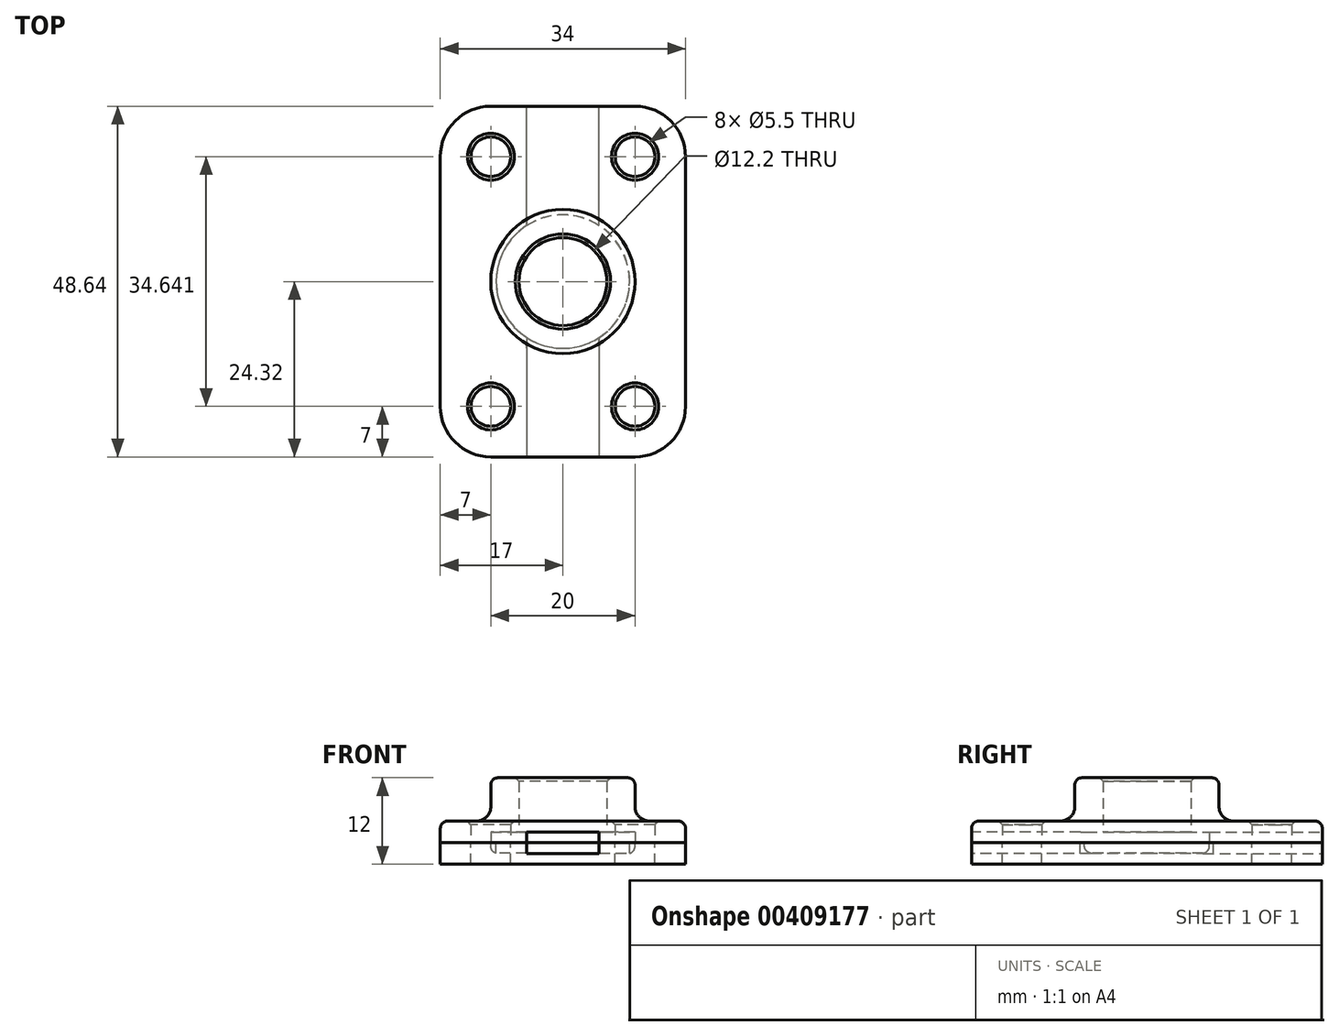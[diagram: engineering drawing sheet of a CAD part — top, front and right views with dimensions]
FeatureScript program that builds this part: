
annotation { "Feature Type Name" : "Feature", "Feature Type Description" : "" }
export const myFeature = defineFeature(function(context is Context, id is Id, definition is map)
    precondition{}
    {
        {
            var Q0;
            Q0=qCreatedBy(makeId("Top.planeOp"),FACE);
            var sketch = newSketch(context, id + "F0", { "sketchPlane" : qUnion([Q0])});
            skCircle(sketch, "E0", {"center": v(-20, 0) * mm, "radius": 2.75 * mm});
            skCircle(sketch, "E1", {"center": v(-10, 17.32) * mm, "radius": 10 * mm});
            skCircle(sketch, "E2", {"center": v(-10, 17.32) * mm, "radius": 6.1 * mm});
            skCircle(sketch, "E3", {"center": v(-10, 17.32) * mm, "radius": 5 * mm});
            skLineSegment(sketch, "E4", {"start": v(-20, 0) * mm, "end": v(-10, 17.32) * mm, "construction": true});
            skLineSegment(sketch, "E5", {"start": v(-10, 17.32) * mm, "end": v(0, 0) * mm, "construction": true});
            skLineSegment(sketch, "E6", {"start": v(-20, 0) * mm, "end": v(0, 0) * mm, "construction": true});
            skArc(sketch, "E7", {"start": v(-27, 0) * mm, "mid": v(-24.95, -4.95) * mm, "end": v(-20, -7) * mm});
            skLineSegment(sketch, "E8", {"start": v(-10, 17.32) * mm, "end": v(-10, 0) * mm, "construction": true});
            skLineSegment(sketch, "E9", {"start": v(-27, 17.32) * mm, "end": v(-27, 0) * mm});
            skLineSegment(sketch, "E10", {"start": v(-20, -7) * mm, "end": v(-10, -7) * mm});
            skLineSegment(sketch, "E11", {"start": v(-15, 8.66) * mm, "end": v(-15, -7) * mm});
            skLineSegment(sketch, "E12.MirrorCS", {"start": v(-5, 8.66) * mm, "end": v(-5, -7) * mm});
            skCircle(sketch, "E13", {"center": v(-10, 17.32) * mm, "radius": 9.25 * mm});
            skLineSegment(sketch, "E14.MirrorCS", {"start": v(0, 0) * mm, "end": v(-10, 17.32) * mm, "construction": true});
            skArc(sketch, "E15.MirrorCS", {"start": v(7, 0) * mm, "mid": v(4.95, -4.95) * mm, "end": v(0, -7) * mm});
            skLineSegment(sketch, "E16.MirrorCS", {"start": v(0, -7) * mm, "end": v(-10, -7) * mm});
            skLineSegment(sketch, "E17.MirrorCS", {"start": v(7, 17.32) * mm, "end": v(7, 0) * mm});
            skCircle(sketch, "E18.MirrorC", {"center": v(0, 0) * mm, "radius": 2.75 * mm});
            skLineSegment(sketch, "E19", {"start": v(-27, 17.32) * mm, "end": v(-10, 17.32) * mm, "construction": true});
            skLineSegment(sketch, "E20.MirrorCS", {"start": v(-27, 17.32) * mm, "end": v(-27, 34.64) * mm});
            skArc(sketch, "E21.MirrorCS", {"start": v(-27, 34.64) * mm, "mid": v(-24.95, 39.6) * mm, "end": v(-20, 41.64) * mm});
            skCircle(sketch, "E22.MirrorC", {"center": v(-20, 34.64) * mm, "radius": 2.75 * mm});
            skLineSegment(sketch, "E23.MirrorCS", {"start": v(-15, 25.98) * mm, "end": v(-15, 41.64) * mm});
            skLineSegment(sketch, "E24.MirrorCS", {"start": v(-5, 25.98) * mm, "end": v(-5, 41.64) * mm});
            skCircle(sketch, "E25.MirrorC", {"center": v(0, 34.64) * mm, "radius": 2.75 * mm});
            skLineSegment(sketch, "E26.MirrorCS", {"start": v(7, 17.32) * mm, "end": v(7, 34.64) * mm});
            skArc(sketch, "E27.MirrorCS", {"start": v(7, 34.64) * mm, "mid": v(4.95, 39.6) * mm, "end": v(0, 41.64) * mm});
            skLineSegment(sketch, "E28.MirrorCS", {"start": v(-20, 41.64) * mm, "end": v(-10, 41.64) * mm});
            skLineSegment(sketch, "E29.MirrorCS", {"start": v(0, 41.64) * mm, "end": v(-10, 41.64) * mm});
            skSolve(sketch);
        }
        {
            var Q0;
            Q0=makeQuery(id+"F0.imprint","IMPRINT",FACE,{"disambiguationData":[TD([[makeQuery(id+"F0.imprint","IMPRINT",EDGE,{"derivedFrom":sQuery(id+"F0.wireOp",EDGE,"E0")}),-1.0]])]});
            var Q1;
            Q1=makeQuery(id+"F0.imprint","IMPRINT",FACE,{"disambiguationData":[TD([[makeQuery(id+"F0.imprint","IMPRINT",EDGE,{"derivedFrom":sQuery(id+"F0.wireOp",EDGE,"E1")}),1.0]])]});
            var Q2;
            {var subQ0=sQuery(id+"F0.wireOp",EDGE,"E11");Q2=makeQuery(id+"F0.imprint","IMPRINT",FACE,{"disambiguationData":[TD([[makeQuery(id+"F0.imprint","IMPRINT",EDGE,{"derivedFrom":subQ0}),1.0]])]});}
            var Q3;
            {var subQ1=sQuery(id+"F0.wireOp",EDGE,"E23.MirrorCS");Q3=makeQuery(id+"F0.imprint","IMPRINT",FACE,{"disambiguationData":[TD([[makeQuery(id+"F0.imprint","IMPRINT",EDGE,{"derivedFrom":subQ1}),-1.0]])]});}
            var Q4;
            {var subQ2=sQuery(id+"F0.wireOp",EDGE,"E12.MirrorCS");Q4=makeQuery(id+"F0.imprint","IMPRINT",FACE,{"disambiguationData":[TD([[makeQuery(id+"F0.imprint","IMPRINT",EDGE,{"derivedFrom":subQ2}),1.0]])]});}
            var Q5;
            Q5=makeQuery(id+"F0.imprint","IMPRINT",FACE,{"disambiguationData":[TD([[makeQuery(id+"F0.imprint","IMPRINT",EDGE,{"derivedFrom":sQuery(id+"F0.wireOp",EDGE,"E2")}),-1.0]])]});
            extrude(context, id + "F1", {"entities" : qUnion([Q0, Q1, Q2, Q3, Q4, Q5]), "depth" : 3 * mm, "offsetDistance" : 25 * mm});
        }
        {
            var Q0;
            Q0=makeQuery(id+"F0.imprint","IMPRINT",FACE,{"disambiguationData":[TD([[makeQuery(id+"F0.imprint","IMPRINT",EDGE,{"derivedFrom":sQuery(id+"F0.wireOp",EDGE,"E1")}),1.0]])]});
            var Q1;
            Q1=makeQuery(id+"F0.imprint","IMPRINT",FACE,{"disambiguationData":[TD([[makeQuery(id+"F0.imprint","IMPRINT",EDGE,{"derivedFrom":sQuery(id+"F0.wireOp",EDGE,"E2")}),-1.0]])]});
            extrude(context, id + "F2", {"entities" : qUnion([Q0, Q1]), "operationType" : NewBodyOperationType.ADD, "depth" : 9 * mm, "offsetDistance" : 25 * mm});
        }
        {
            var Q0;
            Q0=makeQuery(id+"F0.imprint","IMPRINT",FACE,{"disambiguationData":[TD([[makeQuery(id+"F0.imprint","IMPRINT",EDGE,{"derivedFrom":sQuery(id+"F0.wireOp",EDGE,"E2")}),-1.0]])]});
            var Q1;
            {var subQ0=sQuery(id+"F0.wireOp",EDGE,"E11");Q1=makeQuery(id+"F0.imprint","IMPRINT",FACE,{"disambiguationData":[TD([[makeQuery(id+"F0.imprint","IMPRINT",EDGE,{"derivedFrom":subQ0}),1.0]])]});}
            var Q2;
            Q2=makeQuery(id+"F0.imprint","IMPRINT",FACE,{"disambiguationData":[TD([[makeQuery(id+"F0.imprint","IMPRINT",EDGE,{"derivedFrom":sQuery(id+"F0.wireOp",EDGE,"E13")}),-1.0]])]});
            var Q3;
            {var subQ1=sQuery(id+"F0.wireOp",EDGE,"E23.MirrorCS");Q3=makeQuery(id+"F0.imprint","IMPRINT",FACE,{"disambiguationData":[TD([[makeQuery(id+"F0.imprint","IMPRINT",EDGE,{"derivedFrom":subQ1}),-1.0]])]});}
            extrude(context, id + "F3", {"entities" : qUnion([Q0, Q1, Q2, Q3]), "operationType" : NewBodyOperationType.REMOVE, "depth" : 1.5 * mm, "offsetDistance" : 25 * mm});
        }
        {
            var Q0;
            Q0=makeQuery(id+"F2.opExtrude","CAP_EDGE",EDGE,{"disambiguationData":[OSD([sQuery(id+"F0.wireOp",EDGE,"E2")])],"isStart":false});
            var Q1;
            Q1=makeQuery(id+"F1.opExtrude","CAP_EDGE",EDGE,{"disambiguationData":[OSD([sQuery(id+"F0.wireOp",EDGE,"E0")])],"isStart":false});
            var Q2;
            Q2=makeQuery(id+"F1.opExtrude","CAP_EDGE",EDGE,{"disambiguationData":[OSD([sQuery(id+"F0.wireOp",EDGE,"M7DjQCVk-RdmV-3Hag-MnrL-rbCDdXIXaqB2")])],"isStart":false});
            var Q3;
            Q3=makeQuery(id+"F1.opExtrude","CAP_EDGE",EDGE,{"disambiguationData":[OSD([sQuery(id+"F0.wireOp",EDGE,"E22.MirrorC")])],"isStart":false});
            var Q4;
            Q4=makeQuery(id+"F1.opExtrude","CAP_EDGE",EDGE,{"disambiguationData":[OSD([sQuery(id+"F0.wireOp",EDGE,"E25.MirrorC")])],"isStart":false});
            var Q5;
            Q5=makeQuery(id+"F1.opExtrude","CAP_EDGE",EDGE,{"disambiguationData":[OSD([sQuery(id+"F0.wireOp",EDGE,"E18.MirrorC")])],"isStart":false});
            chamfer(context, id + "F4", {"entities" : qUnion([Q0, Q1, Q2, Q3, Q4, Q5]), "width" : 0.5 * mm, "tangentPropagation" : true});
        }
        {
            var Q0;
            Q0=makeQuery(id+"F0.imprint","IMPRINT",FACE,{"disambiguationData":[TD([[makeQuery(id+"F0.imprint","IMPRINT",EDGE,{"derivedFrom":sQuery(id+"F0.wireOp",EDGE,"E0")}),-1.0]])]});
            var Q1;
            {var subQ0=sQuery(id+"F0.wireOp",EDGE,"E11");Q1=makeQuery(id+"F0.imprint","IMPRINT",FACE,{"disambiguationData":[TD([[makeQuery(id+"F0.imprint","IMPRINT",EDGE,{"derivedFrom":subQ0}),1.0]])]});}
            var Q2;
            Q2=makeQuery(id+"F0.imprint","IMPRINT",FACE,{"disambiguationData":[TD([[makeQuery(id+"F0.imprint","IMPRINT",EDGE,{"derivedFrom":sQuery(id+"F0.wireOp",EDGE,"E2")}),-1.0]])]});
            var Q3;
            Q3=makeQuery(id+"F0.imprint","IMPRINT",FACE,{"disambiguationData":[TD([[makeQuery(id+"F0.imprint","IMPRINT",EDGE,{"derivedFrom":sQuery(id+"F0.wireOp",EDGE,"E3")}),1.0]])]});
            var Q4;
            Q4=makeQuery(id+"F0.imprint","IMPRINT",FACE,{"disambiguationData":[TD([[makeQuery(id+"F0.imprint","IMPRINT",EDGE,{"derivedFrom":sQuery(id+"F0.wireOp",EDGE,"E2")}),1.0]])]});
            var Q5;
            Q5=makeQuery(id+"F0.imprint","IMPRINT",FACE,{"disambiguationData":[TD([[makeQuery(id+"F0.imprint","IMPRINT",EDGE,{"derivedFrom":sQuery(id+"F0.wireOp",EDGE,"E13")}),-1.0]])]});
            var Q6;
            {var subQ1=sQuery(id+"F0.wireOp",EDGE,"E23.MirrorCS");Q6=makeQuery(id+"F0.imprint","IMPRINT",FACE,{"disambiguationData":[TD([[makeQuery(id+"F0.imprint","IMPRINT",EDGE,{"derivedFrom":subQ1}),-1.0]])]});}
            var Q7;
            {var subQ2=sQuery(id+"F0.wireOp",EDGE,"E12.MirrorCS");Q7=makeQuery(id+"F0.imprint","IMPRINT",FACE,{"disambiguationData":[TD([[makeQuery(id+"F0.imprint","IMPRINT",EDGE,{"derivedFrom":subQ2}),1.0]])]});}
            extrude(context, id + "F5", {"entities" : qUnion([Q0, Q1, Q2, Q3, Q4, Q5, Q6, Q7]), "oppositeDirection" : true, "depth" : 3 * mm, "offsetDistance" : 25 * mm});
        }
        {
            var Q0;
            {var subQ0=sQuery(id+"F0.wireOp",EDGE,"E11");Q0=makeQuery(id+"F0.imprint","IMPRINT",FACE,{"disambiguationData":[TD([[makeQuery(id+"F0.imprint","IMPRINT",EDGE,{"derivedFrom":subQ0}),1.0]])]});}
            var Q1;
            Q1=makeQuery(id+"F0.imprint","IMPRINT",FACE,{"disambiguationData":[TD([[makeQuery(id+"F0.imprint","IMPRINT",EDGE,{"derivedFrom":sQuery(id+"F0.wireOp",EDGE,"E13")}),-1.0]])]});
            var Q2;
            {var subQ1=sQuery(id+"F0.wireOp",EDGE,"E23.MirrorCS");Q2=makeQuery(id+"F0.imprint","IMPRINT",FACE,{"disambiguationData":[TD([[makeQuery(id+"F0.imprint","IMPRINT",EDGE,{"derivedFrom":subQ1}),-1.0]])]});}
            extrude(context, id + "F6", {"entities" : qUnion([Q0, Q1, Q2]), "operationType" : NewBodyOperationType.REMOVE, "oppositeDirection" : true, "depth" : 1.5 * mm, "offsetDistance" : 25 * mm});
        }
        {
            var Q0;
            Q0=makeQuery(id+"F2.boolean.opBoolean","INTERSECT",EDGE,{"derivedFrom":[makeQuery(id+"F1.opExtrude","CAP_FACE",FACE,{"disambiguationData":[OSD([sQuery(id+"F0.wireOp",EDGE,"E0"),sQuery(id+"F0.wireOp",EDGE,"E2"),sQuery(id+"F0.wireOp",EDGE,"M7DjQCVk-RdmV-3Hag-MnrL-rbCDdXIXaqB2"),sQuery(id+"F0.wireOp",EDGE,"E7"),sQuery(id+"F0.wireOp",EDGE,"vTTUK6wD-1rki-MkEa-Snrt-uhQ54I2DBWBJ"),sQuery(id+"F0.wireOp",EDGE,"E9"),sQuery(id+"F0.wireOp",EDGE,"caf4d550-849c-44d5-98c3-947d7a4541f20.MirrorC"),sQuery(id+"F0.wireOp",EDGE,"9f394b66-eea1-4626-9a4b-a5357dff60b50.MirrorCS"),sQuery(id+"F0.wireOp",EDGE,"E10")])],"isStart":false}),makeQuery(id+"F2.opExtrude","SWEPT_FACE",FACE,{"disambiguationData":[OSD([sQuery(id+"F0.wireOp",EDGE,"E1")])]})]});
            var Q1;
            Q1=makeQuery(id+"F3.boolean.opBoolean","COPY",EDGE,{"derivedFrom":makeQuery(id+"F3.opExtrude","SWEPT_EDGE",EDGE,{"disambiguationData":[OSD([sQuery(id+"F0.wireOp",EDGE,"E12.MirrorCS"),sQuery(id+"F0.wireOp",EDGE,"E16.MirrorCS")])]})});
            var Q2;
            Q2=makeQuery(id+"F3.boolean.opBoolean","COPY",EDGE,{"derivedFrom":makeQuery(id+"F3.opExtrude","SWEPT_EDGE",EDGE,{"disambiguationData":[OSD([sQuery(id+"F0.wireOp",EDGE,"E10"),sQuery(id+"F0.wireOp",EDGE,"E11")])]})});
            var Q3;
            Q3=makeQuery(id+"F3.boolean.opBoolean","COPY",EDGE,{"derivedFrom":makeQuery(id+"F3.opExtrude","SWEPT_EDGE",EDGE,{"disambiguationData":[OSD([sQuery(id+"F0.wireOp",EDGE,"E23.MirrorCS"),sQuery(id+"F0.wireOp",EDGE,"E28.MirrorCS")])]})});
            var Q4;
            Q4=makeQuery(id+"F3.boolean.opBoolean","COPY",EDGE,{"derivedFrom":makeQuery(id+"F3.opExtrude","SWEPT_EDGE",EDGE,{"disambiguationData":[OSD([sQuery(id+"F0.wireOp",EDGE,"E24.MirrorCS"),sQuery(id+"F0.wireOp",EDGE,"E29.MirrorCS")])]})});
            var Q5;
            Q5=makeQuery(id+"F6.boolean.opBoolean","COPY",EDGE,{"derivedFrom":makeQuery(id+"F6.opExtrude","SWEPT_EDGE",EDGE,{"disambiguationData":[OSD([sQuery(id+"F0.wireOp",EDGE,"E23.MirrorCS"),sQuery(id+"F0.wireOp",EDGE,"E28.MirrorCS")])]})});
            var Q6;
            Q6=makeQuery(id+"F6.boolean.opBoolean","COPY",EDGE,{"derivedFrom":makeQuery(id+"F6.opExtrude","SWEPT_EDGE",EDGE,{"disambiguationData":[OSD([sQuery(id+"F0.wireOp",EDGE,"E24.MirrorCS"),sQuery(id+"F0.wireOp",EDGE,"E29.MirrorCS")])]})});
            var Q7;
            Q7=makeQuery(id+"F6.boolean.opBoolean","COPY",EDGE,{"derivedFrom":makeQuery(id+"F6.opExtrude","SWEPT_EDGE",EDGE,{"disambiguationData":[OSD([sQuery(id+"F0.wireOp",EDGE,"E10"),sQuery(id+"F0.wireOp",EDGE,"E11")])]})});
            var Q8;
            Q8=makeQuery(id+"F6.boolean.opBoolean","COPY",EDGE,{"derivedFrom":makeQuery(id+"F6.opExtrude","SWEPT_EDGE",EDGE,{"disambiguationData":[OSD([sQuery(id+"F0.wireOp",EDGE,"E12.MirrorCS"),sQuery(id+"F0.wireOp",EDGE,"E16.MirrorCS")])]})});
            fillet(context, id + "F7", {"entities" : qUnion([Q0, Q1, Q2, Q3, Q4, Q5, Q6, Q7, Q8]), "radius" : 2 * mm, "tangentPropagation" : true, "allowEdgeOverflow" : false});
        }
        {
            var Q0;
            Q0=makeQuery(id+"F1.opExtrude","CAP_EDGE",EDGE,{"disambiguationData":[OSD([sQuery(id+"F0.wireOp",EDGE,"E7")])],"isStart":false});
            var Q1;
            Q1=makeQuery(id+"F3.boolean.opBoolean","COPY",EDGE,{"derivedFrom":makeQuery(id+"F3.opExtrude","SWEPT_EDGE",EDGE,{"disambiguationData":[OSD([sQuery(id+"F0.wireOp",EDGE,"E1"),sQuery(id+"F0.wireOp",EDGE,"E11")])]})});
            var Q2;
            Q2=makeQuery(id+"F3.boolean.opBoolean","COPY",EDGE,{"derivedFrom":makeQuery(id+"F3.opExtrude","SWEPT_EDGE",EDGE,{"disambiguationData":[OSD([sQuery(id+"F0.wireOp",EDGE,"E1"),sQuery(id+"F0.wireOp",EDGE,"E12.MirrorCS")])]})});
            var Q3;
            Q3=makeQuery(id+"F2.opExtrude","CAP_EDGE",EDGE,{"disambiguationData":[OSD([sQuery(id+"F0.wireOp",EDGE,"E1")])],"isStart":false});
            var Q4;
            Q4=makeQuery(id+"F6.boolean.opBoolean","COPY",EDGE,{"derivedFrom":makeQuery(id+"F6.opExtrude","CAP_EDGE",EDGE,{"disambiguationData":[OSD([sQuery(id+"F0.wireOp",EDGE,"E1")])],"isStart":false})});
            fillet(context, id + "F8", {"entities" : qUnion([Q0, Q1, Q2, Q3, Q4]), "radius" : 1 * mm, "tangentPropagation" : true, "allowEdgeOverflow" : false});
        }
    });
